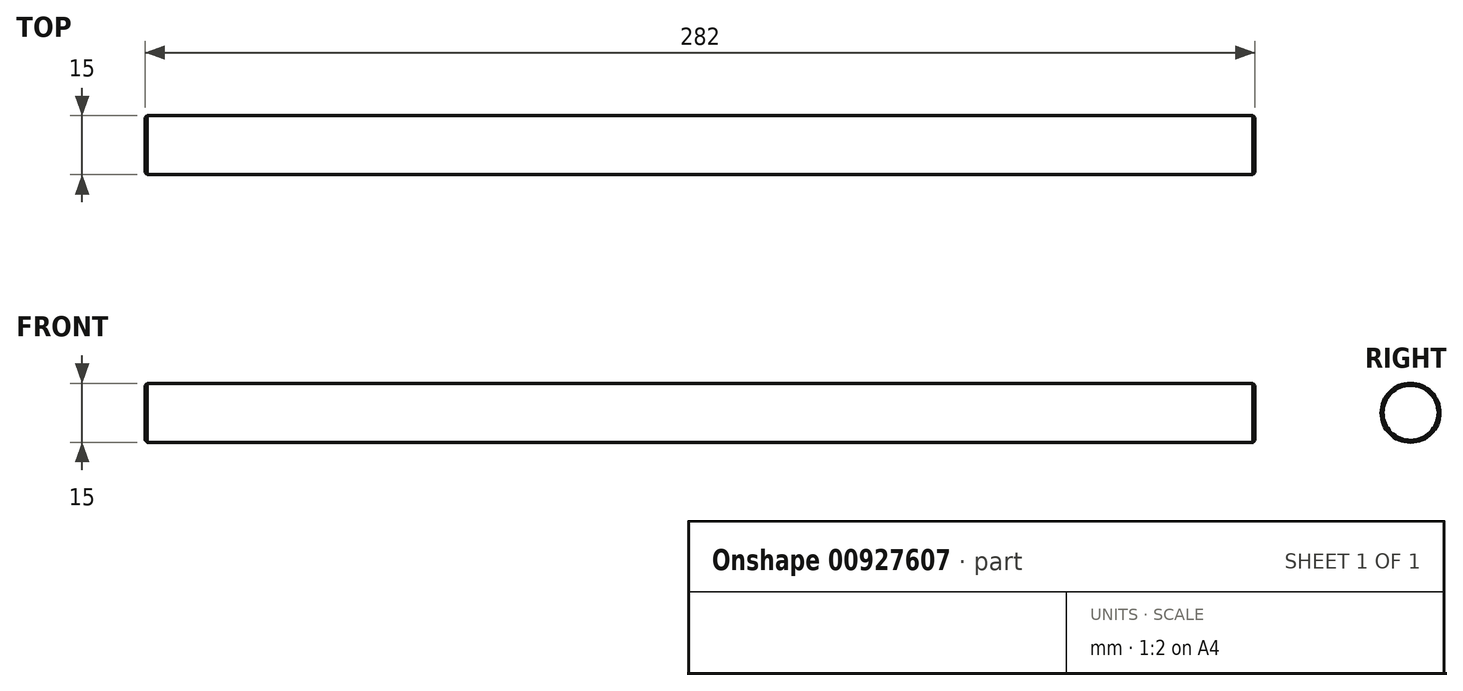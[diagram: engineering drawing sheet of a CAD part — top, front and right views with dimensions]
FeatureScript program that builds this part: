
annotation { "Feature Type Name" : "Feature", "Feature Type Description" : "" }
export const myFeature = defineFeature(function(context is Context, id is Id, definition is map)
    precondition{}
    {
        {
            var Q0;
            Q0=qCreatedBy(makeId("Right.planeOp"),FACE);
            var sketch = newSketch(context, id + "F0", { "sketchPlane" : qUnion([Q0])});
            skCircle(sketch, "E0", {"center": v(0, 0) * mm, "radius": 7.5 * mm});
            skSolve(sketch);
        }
        {
            var Q0;
            Q0 = qSketchRegion(id + "F0", true);
            extrude(context, id + "F1", {"entities" : qUnion([Q0]), "oppositeDirection" : true, "depth" : (244 + 38) * mm, "offsetDistance" : 25 * mm});
        }
        {
            var Q0;
            Q0=makeQuery(id+"F1.opExtrude","CAP_EDGE",EDGE,{"disambiguationData":[OSD([sQuery(id+"F0.wireOp",EDGE,"E0")])],"isStart":true});
            var Q1;
            Q1=makeQuery(id+"F1.opExtrude","CAP_EDGE",EDGE,{"disambiguationData":[OSD([sQuery(id+"F0.wireOp",EDGE,"E0")])],"isStart":false});
            chamfer(context, id + "F2", {"entities" : qUnion([Q0, Q1]), "width" : 0.5 * mm, "tangentPropagation" : true});
        }
    });
